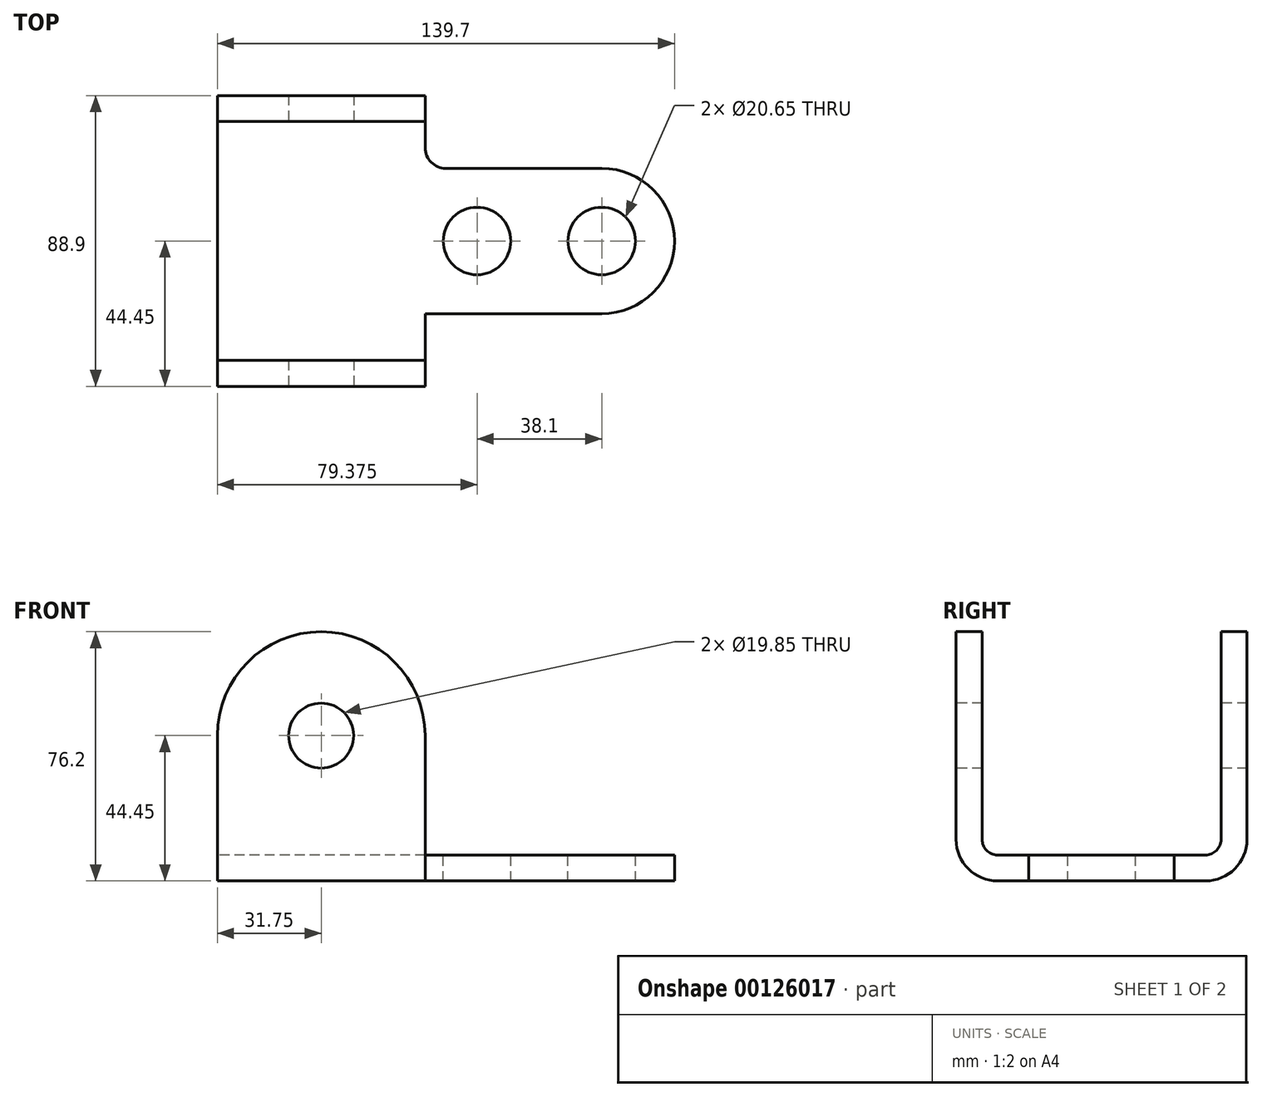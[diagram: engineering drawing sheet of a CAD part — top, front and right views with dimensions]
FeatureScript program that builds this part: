
annotation { "Feature Type Name" : "Feature", "Feature Type Description" : "" }
export const myFeature = defineFeature(function(context is Context, id is Id, definition is map)
    precondition{}
    {
        {
            var Q0;
            Q0=qCreatedBy(makeId("Right.planeOp"),FACE);
            var sketch = newSketch(context, id + "F0", { "sketchPlane" : qUnion([Q0])});
            skLineSegment(sketch, "E0", {"start": v(0, 0) * mm, "end": v(0, 85.68) * mm, "construction": true});
            skLineSegment(sketch, "E1", {"start": v(-44.45, 44.45) * mm, "end": v(-44.45, 12.7) * mm});
            skLineSegment(sketch, "E2", {"start": v(-31.75, 0) * mm, "end": v(0, 0) * mm});
            skLineSegment(sketch, "E3", {"start": v(-44.45, 44.45) * mm, "end": v(-36.51, 44.45) * mm});
            skLineSegment(sketch, "E4", {"start": v(-36.51, 44.45) * mm, "end": v(-36.51, 12.7) * mm});
            skLineSegment(sketch, "E5", {"start": v(-31.75, 7.94) * mm, "end": v(0, 7.94) * mm});
            skPoint(sketch, "E6.visualSharp", {"position": v(-44.45, 0) * mm});
            skArc(sketch, "E6.filletArc", {"start": v(-44.45, 12.7) * mm, "mid": v(-40.73, 3.72) * mm, "end": v(-31.75, 0) * mm});
            skPoint(sketch, "E7.visualSharp", {"position": v(-36.51, 7.94) * mm});
            skArc(sketch, "E7.filletArc", {"start": v(-36.51, 12.7) * mm, "mid": v(-35.12, 9.33) * mm, "end": v(-31.75, 7.94) * mm});
            skArc(sketch, "E8.MirrorCS", {"start": v(36.51, 12.7) * mm, "mid": v(35.12, 9.33) * mm, "end": v(31.75, 7.94) * mm});
            skArc(sketch, "E9.MirrorCS", {"start": v(44.45, 12.7) * mm, "mid": v(40.73, 3.72) * mm, "end": v(31.75, 0) * mm});
            skLineSegment(sketch, "E10.MirrorCS", {"start": v(44.45, 44.45) * mm, "end": v(44.45, 12.7) * mm});
            skLineSegment(sketch, "E11.MirrorCS", {"start": v(31.75, 7.94) * mm, "end": v(0, 7.94) * mm});
            skPoint(sketch, "E12.MirrorP", {"position": v(36.51, 7.94) * mm});
            skLineSegment(sketch, "E13.MirrorCS", {"start": v(36.51, 44.45) * mm, "end": v(36.51, 12.7) * mm});
            skLineSegment(sketch, "E14.MirrorCS", {"start": v(0, 7.94) * mm, "end": v(0, 0) * mm});
            skLineSegment(sketch, "E15.MirrorCS", {"start": v(44.45, 44.45) * mm, "end": v(36.51, 44.45) * mm});
            skPoint(sketch, "E16.MirrorP", {"position": v(44.45, 0) * mm});
            skLineSegment(sketch, "E17.MirrorCS", {"start": v(31.75, 0) * mm, "end": v(0, 0) * mm});
            skSolve(sketch);
        }
        {
            var Q0;
            Q0 = qSketchRegion(id + "F0", true);
            extrude(context, id + "F1", {"entities" : qUnion([Q0]), "depth" : 63.5 * mm});
        }
        {
            var Q0;
            Q0=makeQuery(id+"F1.opExtrude","SWEPT_FACE",FACE,{"disambiguationData":[OSD([sQuery(id+"F0.wireOp",EDGE,"E1")])]});
            var sketch = newSketch(context, id + "F2", { "sketchPlane" : qUnion([Q0])});
            skArc(sketch, "E18", {"start": v(63.5, 44.45) * mm, "mid": v(31.75, 76.2) * mm, "end": v(0, 44.45) * mm});
            skLineSegment(sketch, "E19", {"start": v(0, 44.45) * mm, "end": v(63.5, 44.45) * mm});
            skSolve(sketch);
        }
        {
            var Q0;
            Q0 = qSketchRegion(id + "F2", true);
            var Q1;
            Q1=makeQuery(id+"F1.opExtrude","SWEPT_FACE",FACE,{"disambiguationData":[OSD([sQuery(id+"F0.wireOp",EDGE,"E4")])]});
            extrude(context, id + "F3", {"entities" : qUnion([Q0]), "operationType" : NewBodyOperationType.ADD, "endBound" : BoundingType.UP_TO_SURFACE, "oppositeDirection" : true, "endBoundEntityFace" : qUnion([Q1]), "depth" : 25.4 * mm});
        }
        {
            var Q0;
            Q0=makeQuery(id+"F1.opExtrude","SWEPT_FACE",FACE,{"disambiguationData":[OSD([sQuery(id+"F0.wireOp",EDGE,"E10.MirrorCS")])]});
            var sketch = newSketch(context, id + "F4", { "sketchPlane" : qUnion([Q0])});
            skArc(sketch, "E20.0", {"start": v(-63.5, 44.45) * mm, "mid": v(-31.75, 76.2) * mm, "end": v(0, 44.45) * mm});
            skLineSegment(sketch, "E21.0", {"start": v(0, 44.45) * mm, "end": v(-63.5, 44.45) * mm});
            skSolve(sketch);
        }
        {
            var Q0;
            Q0 = qSketchRegion(id + "F4", true);
            var Q1;
            Q1=makeQuery(id+"F1.opExtrude","SWEPT_FACE",FACE,{"disambiguationData":[OSD([sQuery(id+"F0.wireOp",EDGE,"E13.MirrorCS")])]});
            extrude(context, id + "F5", {"entities" : qUnion([Q0]), "operationType" : NewBodyOperationType.ADD, "endBound" : BoundingType.UP_TO_SURFACE, "oppositeDirection" : true, "endBoundEntityFace" : qUnion([Q1]), "depth" : 25.4 * mm});
        }
        {
            var Q0;
            Q0=makeQuery(id+"F1.opExtrude","SWEPT_FACE",FACE,{"disambiguationData":[OSD([sQuery(id+"F0.wireOp",EDGE,"E2"),sQuery(id+"F0.wireOp",EDGE,"E17.MirrorCS")])]});
            var sketch = newSketch(context, id + "F6", { "sketchPlane" : qUnion([Q0])});
            skLineSegment(sketch, "E22", {"start": v(0, 0) * mm, "end": v(171.63, 0) * mm, "construction": true});
            skPoint(sketch, "E22.endSnap0", {"position": v(63.5, 0) * mm});
            skLineSegment(sketch, "E23", {"start": v(63.5, -22.23) * mm, "end": v(117.47, -22.23) * mm});
            skArc(sketch, "E24", {"start": v(117.47, -22.23) * mm, "mid": v(133.2, -15.72) * mm, "end": v(139.7, 0) * mm});
            skLineSegment(sketch, "E25.MirrorCS", {"start": v(63.5, 22.23) * mm, "end": v(117.47, 22.23) * mm});
            skArc(sketch, "E26.MirrorCS", {"start": v(117.47, 22.23) * mm, "mid": v(133.2, 15.72) * mm, "end": v(139.7, 0) * mm});
            skLineSegment(sketch, "E27", {"start": v(63.5, -22.23) * mm, "end": v(63.5, 22.23) * mm});
            skSolve(sketch);
        }
        {
            var Q0;
            Q0 = qSketchRegion(id + "F6", true);
            var Q1;
            Q1=makeQuery(id+"F1.opExtrude","SWEPT_FACE",FACE,{"disambiguationData":[OSD([sQuery(id+"F0.wireOp",EDGE,"E5"),sQuery(id+"F0.wireOp",EDGE,"E11.MirrorCS")])]});
            extrude(context, id + "F7", {"entities" : qUnion([Q0]), "operationType" : NewBodyOperationType.ADD, "endBound" : BoundingType.UP_TO_SURFACE, "oppositeDirection" : true, "endBoundEntityFace" : qUnion([Q1]), "depth" : 25.4 * mm});
        }
        {
            var Q0;
            Q0=makeQuery(id+"F7.opExtrude","SWEPT_EDGE",EDGE,{"disambiguationData":[OSD([sQuery(id+"F0.wireOp",EDGE,"E2"),sQuery(id+"F0.wireOp",EDGE,"E17.MirrorCS"),sQuery(id+"F6.wireOp",EDGE,"E25.MirrorCS"),sQuery(id+"F6.wireOp",EDGE,"E27")])]});
            var Q1;
            Q1=makeQuery(id+"F7.opExtrude","SWEPT_EDGE",EDGE,{"disambiguationData":[OSD([sQuery(id+"F0.wireOp",EDGE,"E2"),sQuery(id+"F0.wireOp",EDGE,"E17.MirrorCS"),sQuery(id+"F6.wireOp",EDGE,"E23"),sQuery(id+"F6.wireOp",EDGE,"E27")])]});
            fillet(context, id + "F8", {"entities" : qUnion([Q0, Q1]), "radius" : 6.35 * mm, "tangentPropagation" : true, "allowEdgeOverflow" : false});
        }
        {
            var Q0;
            Q0=makeQuery(id+"F2.imprint","IMPRINT",FACE,{"disambiguationData":[TD([[makeQuery(id+"F2.imprint","IMPRINT",EDGE,{"derivedFrom":sQuery(id+"F2.wireOp",EDGE,"E18")}),1.0]])]});
            var sketch = newSketch(context, id + "F9", { "sketchPlane" : qUnion([Q0])});
            skCircle(sketch, "E28", {"center": v(31.75, 44.45) * mm, "radius": 9.92 * mm});
            skSolve(sketch);
        }
        {
            var Q0;
            Q0 = qSketchRegion(id + "F9", true);
            extrude(context, id + "F10", {"entities" : qUnion([Q0]), "operationType" : NewBodyOperationType.REMOVE, "endBound" : BoundingType.THROUGH_ALL, "oppositeDirection" : true, "depth" : 25.4 * mm});
        }
        {
            var Q0;
            {var subQ0=sQuery(id+"F0.wireOp",EDGE,"E11.MirrorCS");var subQ1=sQuery(id+"F0.wireOp",EDGE,"E5");Q0=makeQuery(id+"F7.boolean.opBoolean","MERGE",FACE,{"derivedFrom":[makeQuery(id+"F1.opExtrude","SWEPT_FACE",FACE,{"disambiguationData":[OSD([subQ1,subQ0])]}),makeQuery(id+"F7.opExtrude","CAP_FACE",FACE,{"disambiguationData":[OSD([subQ1,subQ0])],"isStart":false})]});}
            var sketch = newSketch(context, id + "F11", { "sketchPlane" : qUnion([Q0])});
            skCircle(sketch, "E29", {"center": v(117.47, 0) * mm, "radius": 10.33 * mm});
            skCircle(sketch, "E30", {"center": v(79.38, 0) * mm, "radius": 10.33 * mm});
            skSolve(sketch);
        }
        {
            var Q0;
            Q0 = qSketchRegion(id + "F11", true);
            extrude(context, id + "F12", {"entities" : qUnion([Q0]), "operationType" : NewBodyOperationType.REMOVE, "endBound" : BoundingType.THROUGH_ALL, "oppositeDirection" : true, "depth" : 25.4 * mm});
        }
    });
